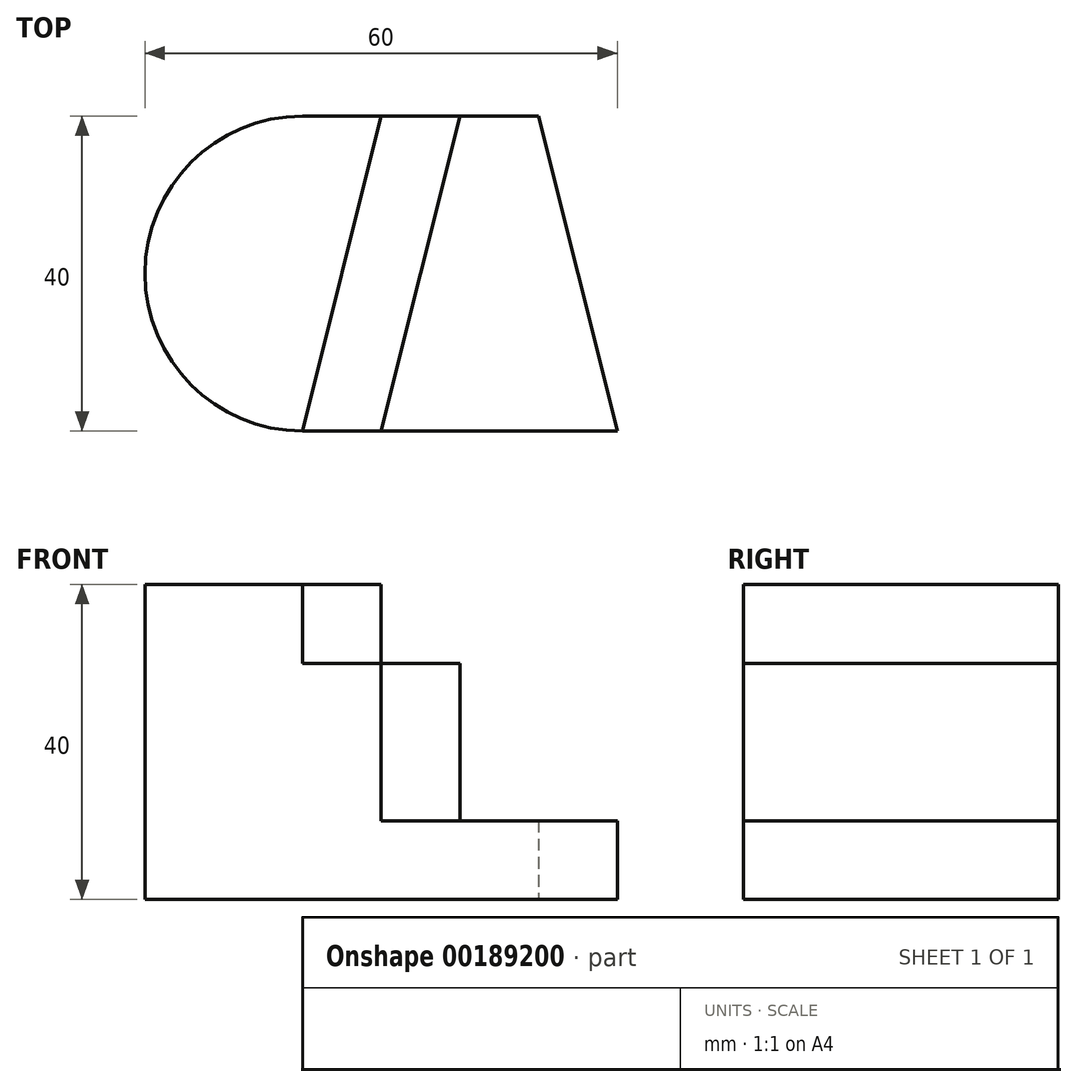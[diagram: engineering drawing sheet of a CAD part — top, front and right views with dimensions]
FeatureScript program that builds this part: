
annotation { "Feature Type Name" : "Feature", "Feature Type Description" : "" }
export const myFeature = defineFeature(function(context is Context, id is Id, definition is map)
    precondition{}
    {
        {
            var Q0;
            Q0=qCreatedBy(makeId("Top.planeOp"),FACE);
            var sketch = newSketch(context, id + "F0", { "sketchPlane" : qUnion([Q0])});
            skLineSegment(sketch, "E0", {"start": v(0, 0) * mm, "end": v(-40, 0) * mm});
            skLineSegment(sketch, "E1", {"start": v(0, 0) * mm, "end": v(-10, 40) * mm});
            skLineSegment(sketch, "E2", {"start": v(-10, 40) * mm, "end": v(-40, 40) * mm});
            skArc(sketch, "E3", {"start": v(-40, 40) * mm, "mid": v(-60, 20) * mm, "end": v(-40, 0) * mm});
            skSolve(sketch);
        }
        {
            var Q0;
            Q0=makeQuery(id+"F0.imprint","IMPRINT",FACE,{"disambiguationData":[TD([[makeQuery(id+"F0.imprint","IMPRINT",EDGE,{"derivedFrom":sQuery(id+"F0.wireOp",EDGE,"E0")}),-1.0]])]});
            extrude(context, id + "F1", {"entities" : qUnion([Q0]), "depth" : 40 * mm});
        }
        {
            var Q0;
            Q0=makeQuery(id+"F1.opExtrude","CAP_FACE",FACE,{"disambiguationData":[OSD([sQuery(id+"F0.wireOp",EDGE,"E0"),sQuery(id+"F0.wireOp",EDGE,"E1"),sQuery(id+"F0.wireOp",EDGE,"E2"),sQuery(id+"F0.wireOp",EDGE,"E3")])],"isStart":false});
            var sketch = newSketch(context, id + "F2", { "sketchPlane" : qUnion([Q0])});
            skLineSegment(sketch, "E4", {"start": v(-30, 40) * mm, "end": v(-40, 0) * mm});
            skLineSegment(sketch, "E5.0", {"start": v(-10, 40) * mm, "end": v(-30, 40) * mm});
            skLineSegment(sketch, "E6.0", {"start": v(0, 0) * mm, "end": v(-10, 40) * mm});
            skLineSegment(sketch, "E7.0", {"start": v(0, 0) * mm, "end": v(-40, 0) * mm});
            skPoint(sketch, "E8.orphan", {"position": v(-40, 40) * mm});
            skSolve(sketch);
        }
        {
            var Q0;
            Q0=makeQuery(id+"F2.imprint","IMPRINT",FACE,{"disambiguationData":[TD([[makeQuery(id+"F2.imprint","IMPRINT",EDGE,{"derivedFrom":sQuery(id+"F2.wireOp",EDGE,"E4")}),1.0]])]});
            extrude(context, id + "F3", {"entities" : qUnion([Q0]), "operationType" : NewBodyOperationType.REMOVE, "oppositeDirection" : true, "depth" : 10 * mm});
        }
        {
            var Q0;
            Q0=makeQuery(id+"F3.boolean.opBoolean","COPY",FACE,{"derivedFrom":makeQuery(id+"F3.opExtrude","CAP_FACE",FACE,{"disambiguationData":[OSD([sQuery(id+"F2.wireOp",EDGE,"E4"),sQuery(id+"F2.wireOp",EDGE,"E5.0"),sQuery(id+"F2.wireOp",EDGE,"E6.0"),sQuery(id+"F2.wireOp",EDGE,"E7.0")])],"isStart":false})});
            var sketch = newSketch(context, id + "F4", { "sketchPlane" : qUnion([Q0])});
            skLineSegment(sketch, "E9", {"start": v(-20, 40) * mm, "end": v(-30, 0) * mm});
            skLineSegment(sketch, "E10.0", {"start": v(-10, 40) * mm, "end": v(-20, 40) * mm});
            skLineSegment(sketch, "E11.0", {"start": v(0, 0) * mm, "end": v(-10, 40) * mm});
            skLineSegment(sketch, "E12.0", {"start": v(0, 0) * mm, "end": v(-30, 0) * mm});
            skPoint(sketch, "E13.orphan", {"position": v(-40, 0) * mm});
            skPoint(sketch, "E14.orphan", {"position": v(-30, 40) * mm});
            skSolve(sketch);
        }
        {
            var Q0;
            Q0=makeQuery(id+"F4.imprint","IMPRINT",FACE,{"disambiguationData":[TD([[makeQuery(id+"F4.imprint","IMPRINT",EDGE,{"derivedFrom":sQuery(id+"F4.wireOp",EDGE,"E9")}),1.0]])]});
            extrude(context, id + "F5", {"entities" : qUnion([Q0]), "operationType" : NewBodyOperationType.REMOVE, "oppositeDirection" : true, "depth" : 20 * mm});
        }
    });
